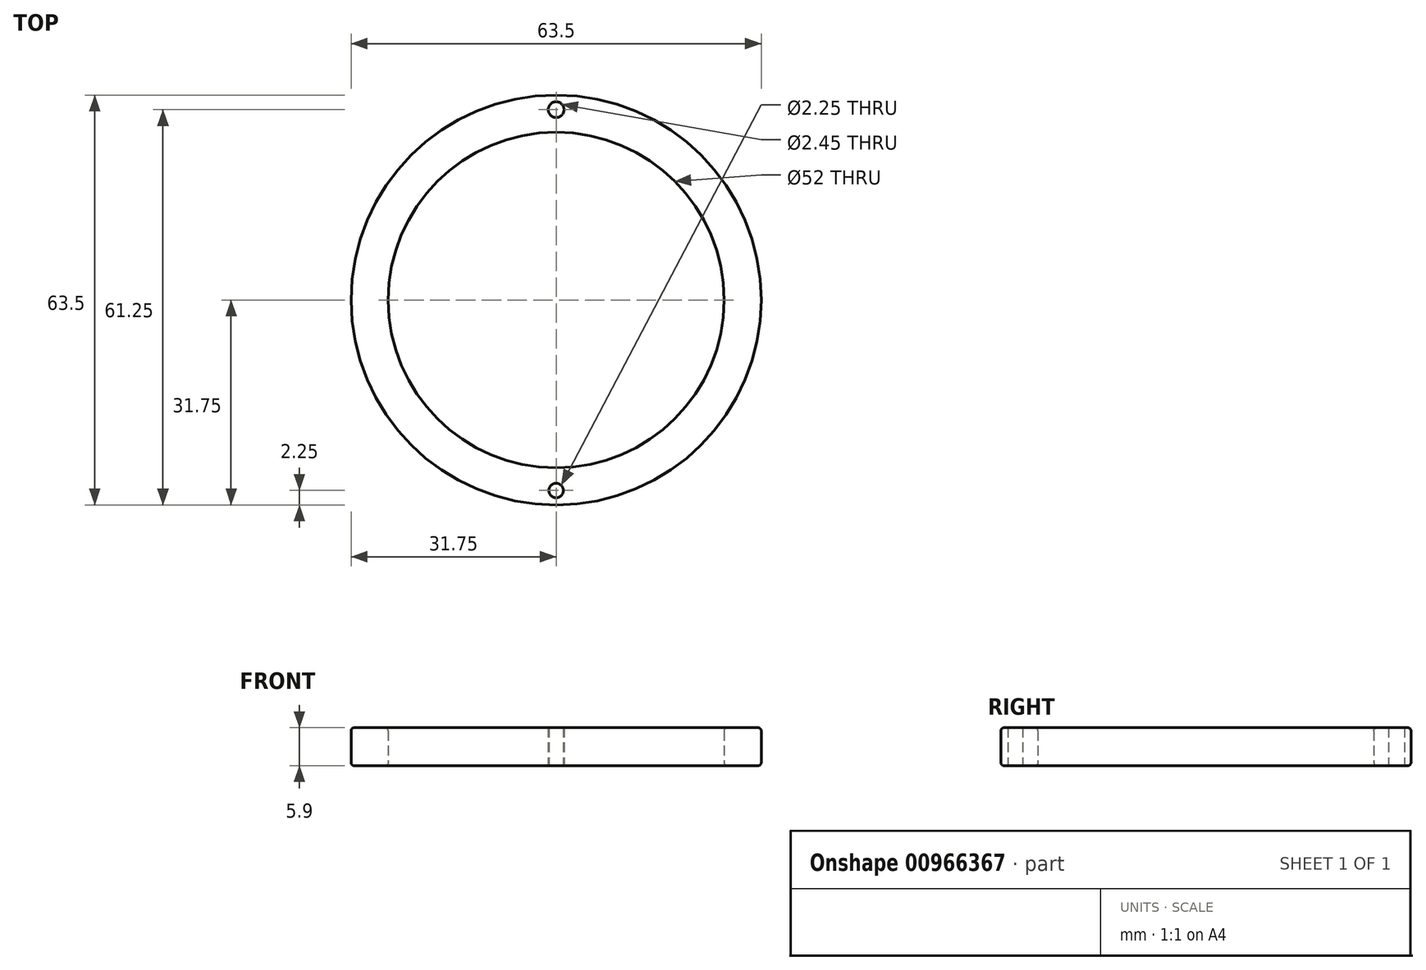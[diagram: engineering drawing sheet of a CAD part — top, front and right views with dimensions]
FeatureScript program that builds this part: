
annotation { "Feature Type Name" : "Feature", "Feature Type Description" : "" }
export const myFeature = defineFeature(function(context is Context, id is Id, definition is map)
    precondition{}
    {
        {
            var Q0;
            Q0=qCreatedBy(makeId("Top.planeOp"),FACE);
            var sketch = newSketch(context, id + "F0", { "sketchPlane" : qUnion([Q0])});
            skCircle(sketch, "E0", {"center": v(0, 0) * mm, "radius": 26 * mm});
            skCircle(sketch, "E1", {"center": v(0, 0) * mm, "radius": 31.75 * mm});
            skPoint(sketch, "E2", {"position": v(0, -29.5) * mm});
            skPoint(sketch, "E3.1.0", {"position": v(0, 29.5) * mm});
            skCircle(sketch, "E4", {"center": v(0, -29.5) * mm, "radius": 1.13 * mm});
            skCircle(sketch, "E5", {"center": v(0, 29.5) * mm, "radius": 1.13 * mm});
            skCircle(sketch, "E6", {"center": v(0, 29.5) * mm, "radius": 1.23 * mm});
            skSolve(sketch);
        }
        {
            var Q0;
            Q0=qSketchRegion(id+"F0",true);
            extrude(context, id + "F1", {"entities" : qUnion([Q0]), "depth" : 5 * mm, "offsetDistance" : 25 * mm});
        }
        {
            var Q0;
            Q0=qSketchRegion(id+"F0",true);
            extrude(context, id + "F2", {"entities" : qUnion([Q0]), "operationType" : NewBodyOperationType.ADD, "depth" : 5.9 * mm, "offsetDistance" : 25 * mm});
        }
        {
            var Q0;
            Q0=makeQuery(id+"F1.opExtrude","CAP_EDGE",EDGE,{"disambiguationData":[OSD([sQuery(id+"F0.wireOp",EDGE,"E0")])],"isStart":true});
            var Q1;
            Q1=makeQuery(id+"F1.opExtrude","CAP_EDGE",EDGE,{"disambiguationData":[OSD([sQuery(id+"F0.wireOp",EDGE,"E1")])],"isStart":true});
            var Q2;
            Q2=makeQuery(id+"F1.opExtrude","CAP_EDGE",EDGE,{"disambiguationData":[OSD([sQuery(id+"F0.wireOp",EDGE,"E1")])],"isStart":false});
            fillet(context, id + "F3", {"entities" : qUnion([Q0, Q1, Q2]), "radius" : .5 * mm, "tangentPropagation" : true, "allowEdgeOverflow" : false});
        }
        {
            var Q0;
            Q0=makeQuery(id+"F2.opExtrude","CAP_EDGE",EDGE,{"disambiguationData":[OSD([sQuery(id+"F0.wireOp",EDGE,"E0")])],"isStart":false});
            var Q1;
            Q1=makeQuery(id+"F2.opExtrude","CAP_EDGE",EDGE,{"disambiguationData":[OSD([sQuery(id+"F0.wireOp",EDGE,"E1")])],"isStart":false});
            fillet(context, id + "F4", {"entities" : qUnion([Q0, Q1]), "radius" : .5 * mm, "tangentPropagation" : true, "allowEdgeOverflow" : false});
        }
    });
